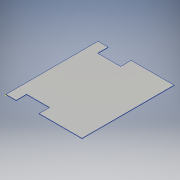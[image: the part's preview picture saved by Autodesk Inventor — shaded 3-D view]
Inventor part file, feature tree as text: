
AUTODESK INVENTOR PART (.ipt)
format: ipt  version: 2018 (Build 220112000, 112)  size: 105,984 bytes
history: native  units: in
note: dims shown in document units (in); Inventor stores cm internally (conversion verified against a paired STEP export)
features: sketch x2, extrude x1
ambient origin geometry x8: Origin, YZ Plane, XZ Plane, XY Plane, X Axis, Y Axis, Z Axis, Center Point
bodies: Solid1 (feature_tree)
feature tree (3):
  sketch  "Sketch1"  dims[d1=22.0in d2=5.5in]
  extrude  "Extrusion1"  Depth=5.5in
  sketch  "Sketch2"  dims[d3=2.438in d4=2.5in d5=0.1in d6=0.0in d8=10.25in]
